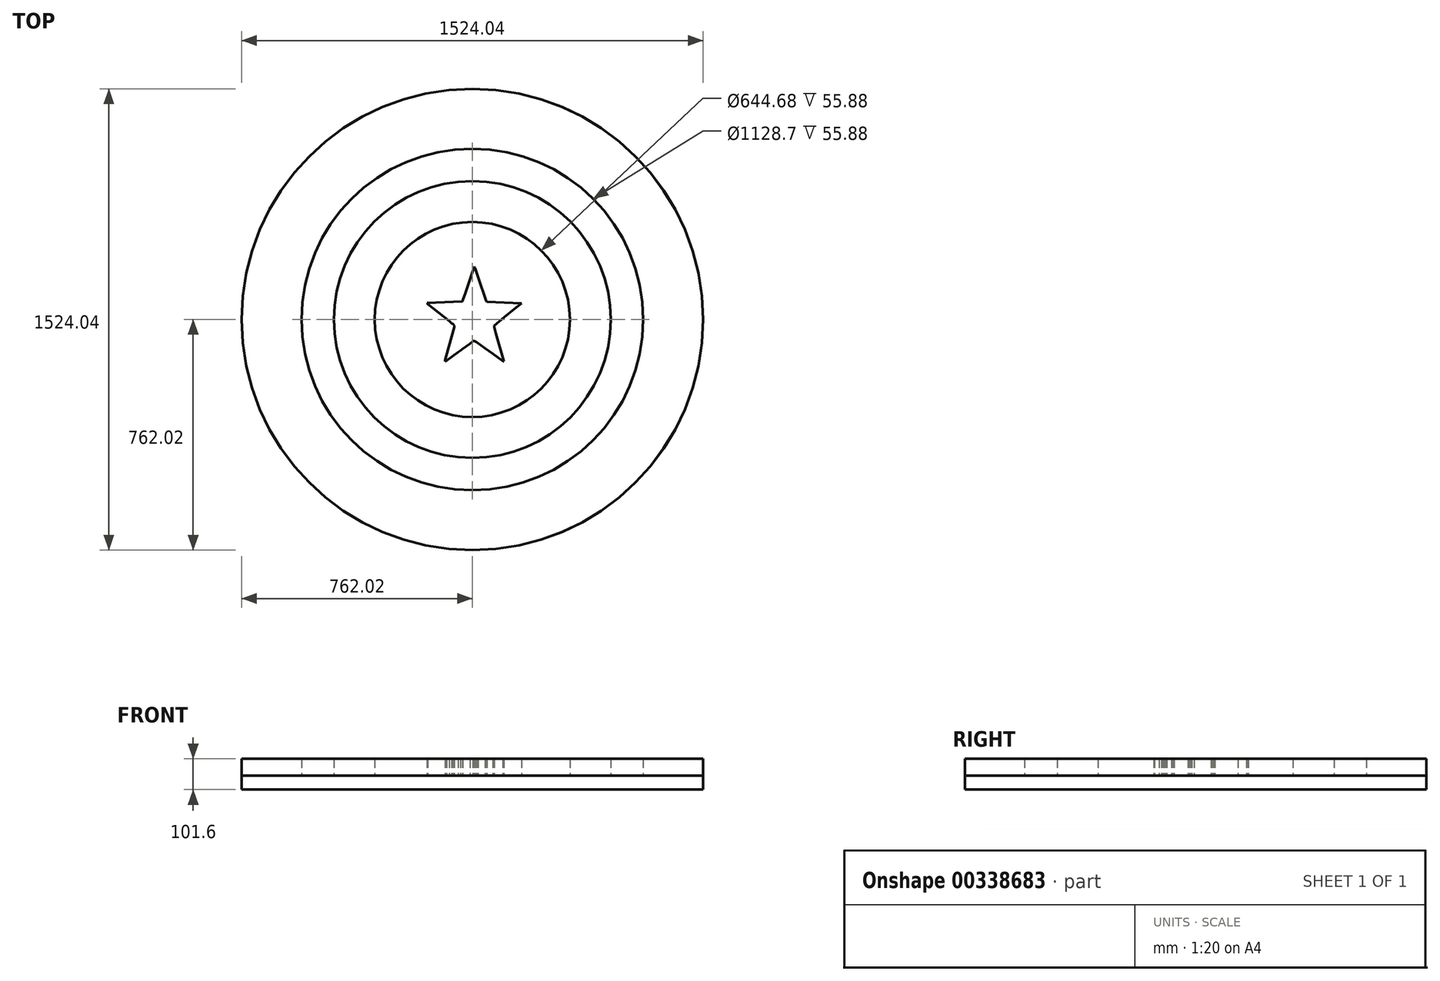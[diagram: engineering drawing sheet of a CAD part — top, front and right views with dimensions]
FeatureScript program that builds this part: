
annotation { "Feature Type Name" : "Feature", "Feature Type Description" : "" }
export const myFeature = defineFeature(function(context is Context, id is Id, definition is map)
    precondition{}
    {
        {
            var Q0;
            Q0=qCreatedBy(makeId("Top.planeOp"),FACE);
            var sketch = newSketch(context, id + "F0", { "sketchPlane" : qUnion([Q0])});
            skCircle(sketch, "E0", {"center": v(0, 0) * mm, "radius": 762 * mm});
            skCircle(sketch, "E1", {"center": v(0, 0) * mm, "radius": 564.35 * mm});
            skCircle(sketch, "E2", {"center": v(0, 0) * mm, "radius": 457.2 * mm});
            skCircle(sketch, "E3", {"center": v(0, 0) * mm, "radius": 694.28 * mm});
            skCircle(sketch, "E4", {"center": v(0, 0) * mm, "radius": 322.34 * mm});
            skCircle(sketch, "E5", {"center": v(0, 0) * mm, "radius": 203.2 * mm});
            skLineSegment(sketch, "E6", {"start": v(-165.1, 60.7) * mm, "end": v(-36.62, 65.1) * mm});
            skLineSegment(sketch, "E7", {"start": v(-36.62, 65.1) * mm, "end": v(-9.92, 144.9) * mm});
            skLineSegment(sketch, "E8", {"start": v(-9.92, 144.9) * mm, "end": v(5.1, 189.62) * mm});
            skLineSegment(sketch, "E9", {"start": v(5.1, 189.62) * mm, "end": v(5.81, 190.23) * mm});
            skLineSegment(sketch, "E10", {"start": v(5.81, 190.23) * mm, "end": v(6.77, 190.5) * mm});
            skLineSegment(sketch, "E11", {"start": v(6.77, 190.5) * mm, "end": v(21.78, 146.65) * mm});
            skLineSegment(sketch, "E12", {"start": v(21.78, 146.65) * mm, "end": v(48.48, 67.72) * mm});
            skLineSegment(sketch, "E13", {"start": v(48.48, 67.72) * mm, "end": v(49.32, 65.1) * mm});
            skLineSegment(sketch, "E14", {"start": v(49.32, 65.1) * mm, "end": v(177.8, 60.7) * mm});
            skLineSegment(sketch, "E15", {"start": v(177.8, 60.7) * mm, "end": v(177.8, 58.95) * mm});
            skLineSegment(sketch, "E16", {"start": v(177.8, 58.95) * mm, "end": v(142.76, 30.89) * mm});
            skLineSegment(sketch, "E17", {"start": v(142.76, 30.89) * mm, "end": v(107.72, 2.83) * mm});
            skLineSegment(sketch, "E18", {"start": v(107.72, 2.83) * mm, "end": v(77.68, -21.73) * mm});
            skLineSegment(sketch, "E19", {"start": v(77.68, -21.73) * mm, "end": v(76.98, -22.9) * mm});
            skLineSegment(sketch, "E20", {"start": v(76.98, -22.9) * mm, "end": v(76.85, -24.36) * mm});
            skLineSegment(sketch, "E21", {"start": v(76.85, -24.36) * mm, "end": v(103.55, -118.2) * mm});
            skLineSegment(sketch, "E22", {"start": v(103.55, -118.2) * mm, "end": v(112.72, -152.4) * mm});
            skLineSegment(sketch, "E23", {"start": v(112.72, -152.4) * mm, "end": v(110.08, -151.22) * mm});
            skLineSegment(sketch, "E24", {"start": v(110.08, -151.22) * mm, "end": v(107.57, -149.7) * mm});
            skLineSegment(sketch, "E25", {"start": v(107.57, -149.7) * mm, "end": v(102.71, -146.26) * mm});
            skLineSegment(sketch, "E26", {"start": v(102.71, -146.26) * mm, "end": v(69.34, -121.7) * mm});
            skLineSegment(sketch, "E27", {"start": v(69.34, -121.7) * mm, "end": v(30.13, -93.64) * mm});
            skLineSegment(sketch, "E28", {"start": v(30.13, -93.64) * mm, "end": v(7.6, -76.98) * mm});
            skLineSegment(sketch, "E29", {"start": v(7.6, -76.98) * mm, "end": v(5.03, -77.44) * mm});
            skLineSegment(sketch, "E30", {"start": v(5.03, -77.44) * mm, "end": v(2.6, -78.73) * mm});
            skLineSegment(sketch, "E31", {"start": v(2.6, -78.73) * mm, "end": v(-35.78, -106.8) * mm});
            skLineSegment(sketch, "E32", {"start": v(-35.78, -106.8) * mm, "end": v(-42.98, -111.9) * mm});
            skLineSegment(sketch, "E33", {"start": v(-42.98, -111.9) * mm, "end": v(-49.97, -117.32) * mm});
            skLineSegment(sketch, "E34", {"start": v(-49.97, -117.32) * mm, "end": v(-52.6, -118.85) * mm});
            skLineSegment(sketch, "E35", {"start": v(-52.6, -118.85) * mm, "end": v(-54.97, -120.83) * mm});
            skLineSegment(sketch, "E36", {"start": v(-54.97, -120.83) * mm, "end": v(-94.18, -148.9) * mm});
            skLineSegment(sketch, "E37", {"start": v(-94.18, -148.9) * mm, "end": v(-99.19, -152.4) * mm});
            skLineSegment(sketch, "E38", {"start": v(-99.19, -152.4) * mm, "end": v(-100.02, -152.4) * mm});
            skLineSegment(sketch, "E39", {"start": v(-100.02, -152.4) * mm, "end": v(-74.16, -59.44) * mm});
            skLineSegment(sketch, "E40", {"start": v(-74.16, -59.44) * mm, "end": v(-64.15, -24.36) * mm});
            skLineSegment(sketch, "E41", {"start": v(-64.15, -24.36) * mm, "end": v(-64.23, -23) * mm});
            skLineSegment(sketch, "E42", {"start": v(-64.23, -23) * mm, "end": v(-64.98, -21.73) * mm});
            skLineSegment(sketch, "E43", {"start": v(-64.98, -21.73) * mm, "end": v(-99.19, 6.33) * mm});
            skLineSegment(sketch, "E44", {"start": v(-99.19, 6.33) * mm, "end": v(-134.23, 34.4) * mm});
            skLineSegment(sketch, "E45", {"start": v(-134.23, 34.4) * mm, "end": v(-165.1, 58.95) * mm});
            skLineSegment(sketch, "E46", {"start": v(-165.1, 58.95) * mm, "end": v(-165.1, 60.7) * mm});
            skLineSegment(sketch, "E47", {"start": v(-149.25, 54.57) * mm, "end": v(-149, 53.6) * mm});
            skLineSegment(sketch, "E48", {"start": v(-149, 53.6) * mm, "end": v(-148.4, 52.72) * mm});
            skLineSegment(sketch, "E49", {"start": v(-148.4, 52.72) * mm, "end": v(-146.75, 51.06) * mm});
            skLineSegment(sketch, "E50", {"start": v(-146.75, 51.06) * mm, "end": v(-111.7, 23) * mm});
            skLineSegment(sketch, "E51", {"start": v(-111.7, 23) * mm, "end": v(-76.66, -5.07) * mm});
            skLineSegment(sketch, "E52", {"start": v(-76.66, -5.07) * mm, "end": v(-68.32, -12.08) * mm});
            skLineSegment(sketch, "E53", {"start": v(-68.32, -12.08) * mm, "end": v(-63.56, -15.78) * mm});
            skLineSegment(sketch, "E54", {"start": v(-63.56, -15.78) * mm, "end": v(-59.14, -19.98) * mm});
            skLineSegment(sketch, "E55", {"start": v(-59.14, -19.98) * mm, "end": v(-59.14, -25.24) * mm});
            skLineSegment(sketch, "E56", {"start": v(-59.14, -25.24) * mm, "end": v(-85.84, -120.83) * mm});
            skLineSegment(sketch, "E57", {"start": v(-85.84, -120.83) * mm, "end": v(-90.01, -134.86) * mm});
            skLineSegment(sketch, "E58", {"start": v(-90.01, -134.86) * mm, "end": v(-90.01, -138.37) * mm});
            skLineSegment(sketch, "E59", {"start": v(-90.01, -138.37) * mm, "end": v(-85, -135.74) * mm});
            skLineSegment(sketch, "E60", {"start": v(-85, -135.74) * mm, "end": v(-46.63, -107.67) * mm});
            skLineSegment(sketch, "E61", {"start": v(-46.63, -107.67) * mm, "end": v(-39.43, -102.58) * mm});
            skLineSegment(sketch, "E62", {"start": v(-39.43, -102.58) * mm, "end": v(-32.45, -97.15) * mm});
            skLineSegment(sketch, "E63", {"start": v(-32.45, -97.15) * mm, "end": v(-7.42, -79.61) * mm});
            skLineSegment(sketch, "E64", {"start": v(-7.42, -79.61) * mm, "end": v(1.76, -72.6) * mm});
            skLineSegment(sketch, "E65", {"start": v(1.76, -72.6) * mm, "end": v(4.15, -71.3) * mm});
            skLineSegment(sketch, "E66", {"start": v(4.15, -71.3) * mm, "end": v(5.41, -70.87) * mm});
            skLineSegment(sketch, "E67", {"start": v(5.41, -70.87) * mm, "end": v(6.77, -70.84) * mm});
            skLineSegment(sketch, "E68", {"start": v(6.77, -70.84) * mm, "end": v(13.44, -74.35) * mm});
            skLineSegment(sketch, "E69", {"start": v(13.44, -74.35) * mm, "end": v(41.8, -95.4) * mm});
            skLineSegment(sketch, "E70", {"start": v(41.8, -95.4) * mm, "end": v(66.84, -112.94) * mm});
            skLineSegment(sketch, "E71", {"start": v(66.84, -112.94) * mm, "end": v(100.2, -137.5) * mm});
            skLineSegment(sketch, "E72", {"start": v(100.2, -137.5) * mm, "end": v(101.77, -138.2) * mm});
            skLineSegment(sketch, "E73", {"start": v(101.77, -138.2) * mm, "end": v(103.55, -138.37) * mm});
            skLineSegment(sketch, "E74", {"start": v(103.55, -138.37) * mm, "end": v(77.68, -46.29) * mm});
            skLineSegment(sketch, "E75", {"start": v(77.68, -46.29) * mm, "end": v(71.84, -25.24) * mm});
            skLineSegment(sketch, "E76", {"start": v(71.84, -25.24) * mm, "end": v(71.84, -19.98) * mm});
            skLineSegment(sketch, "E77", {"start": v(71.84, -19.98) * mm, "end": v(106.05, 8.09) * mm});
            skLineSegment(sketch, "E78", {"start": v(106.05, 8.09) * mm, "end": v(140.26, 36.15) * mm});
            skLineSegment(sketch, "E79", {"start": v(140.26, 36.15) * mm, "end": v(161.95, 53.7) * mm});
            skLineSegment(sketch, "E80", {"start": v(161.95, 53.7) * mm, "end": v(47.65, 58.95) * mm});
            skLineSegment(sketch, "E81", {"start": v(47.65, 58.95) * mm, "end": v(45.15, 60.7) * mm});
            skLineSegment(sketch, "E82", {"start": v(45.15, 60.7) * mm, "end": v(18.45, 139.64) * mm});
            skLineSegment(sketch, "E83", {"start": v(18.45, 139.64) * mm, "end": v(8.44, 170.33) * mm});
            skLineSegment(sketch, "E84", {"start": v(8.44, 170.33) * mm, "end": v(6.77, 173.84) * mm});
            skLineSegment(sketch, "E85", {"start": v(6.77, 173.84) * mm, "end": v(5.53, 173.22) * mm});
            skLineSegment(sketch, "E86", {"start": v(5.53, 173.22) * mm, "end": v(4.69, 171.67) * mm});
            skLineSegment(sketch, "E87", {"start": v(4.69, 171.67) * mm, "end": v(3.43, 167.7) * mm});
            skLineSegment(sketch, "E88", {"start": v(3.43, 167.7) * mm, "end": v(-23.27, 87.9) * mm});
            skLineSegment(sketch, "E89", {"start": v(-23.27, 87.9) * mm, "end": v(-31.61, 63.34) * mm});
            skLineSegment(sketch, "E90", {"start": v(-31.61, 63.34) * mm, "end": v(-32.19, 61.43) * mm});
            skLineSegment(sketch, "E91", {"start": v(-32.19, 61.43) * mm, "end": v(-33.28, 59.83) * mm});
            skLineSegment(sketch, "E92", {"start": v(-33.28, 59.83) * mm, "end": v(-149.25, 54.57) * mm});
            skSolve(sketch);
        }
        {
            var Q0;
            Q0 = qSketchRegion(id + "F0", true);
            var Q1;
            Q1=makeQuery(id+"F0.imprint","IMPRINT",FACE,{"disambiguationData":[TD([[makeQuery(id+"F0.imprint","IMPRINT",EDGE,{"derivedFrom":sQuery(id+"F0.wireOp",EDGE,"E1")}),-1.0]])]});
            var Q2;
            Q2=makeQuery(id+"F0.imprint","IMPRINT",FACE,{"disambiguationData":[TD([[makeQuery(id+"F0.imprint","IMPRINT",EDGE,{"derivedFrom":sQuery(id+"F0.wireOp",EDGE,"E4")}),-1.0]])]});
            var Q3;
            Q3=makeQuery(id+"F0.imprint","IMPRINT",FACE,{"disambiguationData":[TD([[makeQuery(id+"F0.imprint","IMPRINT",EDGE,{"derivedFrom":sQuery(id+"F0.wireOp",EDGE,"E47")}),1.0]])]});
            extrude(context, id + "F1", {"entities" : qUnion([Q0, Q1, Q2, Q3]), "depth" : 55.88 * mm});
        }
        {
            var Q0;
            Q0=qCreatedBy(makeId("Top.planeOp"),FACE);
            var sketch = newSketch(context, id + "F2", { "sketchPlane" : qUnion([Q0])});
            skCircle(sketch, "E93", {"center": v(0, 0) * mm, "radius": 762.02 * mm});
            skSolve(sketch);
        }
        {
            var Q0;
            Q0 = qSketchRegion(id + "F2", true);
            extrude(context, id + "F3", {"entities" : qUnion([Q0]), "oppositeDirection" : true, "depth" : 45.72 * mm});
        }
    });
